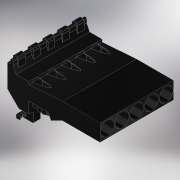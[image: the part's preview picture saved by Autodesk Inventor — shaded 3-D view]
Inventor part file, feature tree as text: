
AUTODESK INVENTOR PART (.ipt)
format: ipt  version: 2018 (Build 220112000, 112)  size: 727,552 bytes
history: native  units: in
note: dims shown in document units (in); Inventor stores cm internally (conversion verified against a paired STEP export)
features: other x15, extrude x15, chamfer x2, fillet x2, pattern_linear x1, sketch x1, projected_geometry x1
ambient origin geometry x8: Origin, YZ Plane, XZ Plane, XY Plane, X Axis, Y Axis, Z Axis, Center Point
bodies: Solid1 (feature_tree)
feature tree (37):
  other  "Base Sketch"
  extrude  "Side Walls"  TaperAngle=0.0deg  [1 undecoded]
  extrude  "Back Wall"  TaperAngle=0.0deg  [1 undecoded]
  extrude  "Front Wall"  TaperAngle=0.0deg  [1 undecoded]
  extrude  "Whistle Housing"  Depth=0.2067in TaperAngle=0.0deg
  extrude  "Tube Socket"  Depth=0.0938in
  other  "Midplane"
  extrude  "Slit"  Depth=0.2067in
  other  "Silicone Fitting"
  extrude  "Silicone Fitting to Chamber"  Depth=0.2067in
  extrude  "Hinge"  Depth=0.2067in
  extrude  "Hinge Nub"  TaperAngle=90.0deg  [1 undecoded]
  chamfer  "Hinge Clearance Chamfer"  Distance=1.5748in
  chamfer  "Spring Pass Chamfer"  Distance=0.3937in
  extrude  "Spring Block"  TaperAngle=0.0deg  [1 undecoded]
  extrude  "Spring Hook"  Depth=0.2067in
  other  "Sping Hook Draft"
  fillet  "Spring Hook Fillet"  Radius=0.4134in
  extrude  "Edge Cut"  TaperAngle=0.0deg  [1 undecoded]
  fillet  "Edge Fillet"  Radius=0.189in
  other  "Pincher Triangle Sketch"
  extrude  "Pincher Triangle"  TaperAngle=0.0deg  [1 undecoded]
  extrude  "Triangle Coupling Male"  Depth=0.2067in
  extrude  "Expand: Triangle Coupling Female"  Depth=0.2067in
  pattern_linear  "Key Repitition"  Spacing1=45.0deg  [1 undecoded]
  sketch  "Sketch5"  dims[d1=0.0in d2=0.0in d3=0.0in d4=0.0in d61=1.5748in d62=0.0in d65=0.0938in d66=0.1181in d67=0.0276in d68=0.0197in d69=90.0deg d71=1.5748in d72=0.0in d78=0.3937in d80=0.0in d81=0.4331in d88=0.4134in d89=0.0in d92=0.189in d93=0.0in d101=0.0079in d105=0.0787in d106=0.1772in d107=45.0deg d112=0.0787in d113=45.0deg d135=0.2067in d136=0.315in d137=0.5906in d139=0.0in d160=0.1181in d161=0.0984in d162=0.3937in d163=0.1575in d164=0.0in d171=1.03in d173=0.4724in d176=0.4134in d177=0.0in d178=0.2067in d179=0.0in d180=0.1374in d181=0.0394in d187=0.2067in d188=0.2362in d190=0.5906in d191=0.0in d193=0.1654in d194=0.0512in d198=0.4134in d199=0.0in d277=0.0079in d278=1.9685in d280=0.4134in d282=0.2067in d283=0.0in d284=0.0394in d285=0.0079in d289=0.0827in d298=0.2067in d299=0.0in d300=0.0787in d301=0.0394in d302=0.0079in d303=0.315in]
  projected_geometry  "Projected Loop2"
  other  "Whistle Housing Sketch"
  other  "Edge Cut Sketch"
  other  "Slit Sketch"
  other  "Silicone Fitting Sketch"
  other  "Silicone Fitting to Chamber Sketch"
  other  "Tube Socket Sketch"
  other  "Hinge Sketch"
  other  "Hinge Nub Sketch"
  other  "Spring Block Sketch"
  other  "Spring Hook Sketch"
note: 8 required parameter values undecoded (feature->parameter linkage not recoverable at this tier; creation-order binding heuristic only, values carry confidence <= 0.55)
